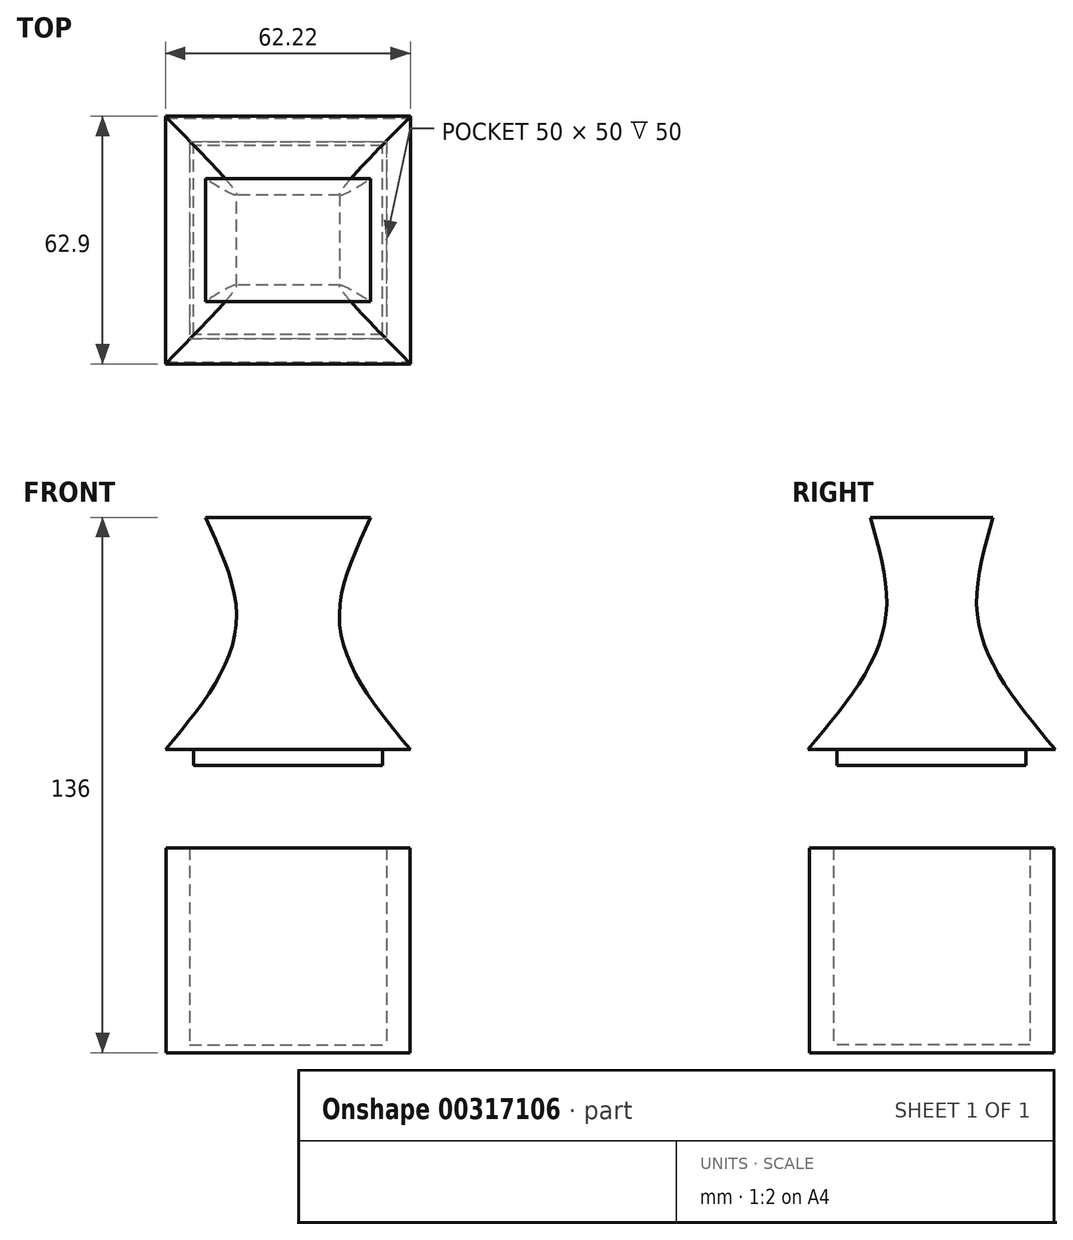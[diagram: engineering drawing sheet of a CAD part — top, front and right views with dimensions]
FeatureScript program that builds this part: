
annotation { "Feature Type Name" : "Feature", "Feature Type Description" : "" }
export const myFeature = defineFeature(function(context is Context, id is Id, definition is map)
    precondition{}
    {
        {
            var Q0;
            Q0=qCreatedBy(makeId("Top.planeOp"),FACE);
            var sketch = newSketch(context, id + "F0", { "sketchPlane" : qUnion([Q0])});
            skLineSegment(sketch, "E0.bottom", {"start": v(-25, 25) * mm, "end": v(25, 25) * mm});
            skLineSegment(sketch, "E0.top", {"start": v(-25, -25) * mm, "end": v(25, -25) * mm});
            skLineSegment(sketch, "E0.left", {"start": v(-25, 25) * mm, "end": v(-25, -25) * mm});
            skLineSegment(sketch, "E0.right", {"start": v(25, 25) * mm, "end": v(25, -25) * mm});
            skPoint(sketch, "E0.middle", {"position": v(0, 0) * mm});
            skLineSegment(sketch, "E1.0", {"start": v(-31, 31) * mm, "end": v(31, 31) * mm});
            skLineSegment(sketch, "E1.1", {"start": v(-31, 31) * mm, "end": v(-31, -31) * mm});
            skLineSegment(sketch, "E1.2", {"start": v(-31, -31) * mm, "end": v(31, -31) * mm});
            skLineSegment(sketch, "E1.3", {"start": v(31, 31) * mm, "end": v(31, -31) * mm});
            skSolve(sketch);
        }
        {
            var Q0;
            Q0=makeQuery(id+"F0.imprint","IMPRINT",FACE,{"disambiguationData":[TD([[makeQuery(id+"F0.imprint","IMPRINT",EDGE,{"derivedFrom":sQuery(id+"F0.wireOp",EDGE,"E0.bottom")}),1.0]])]});
            extrude(context, id + "F1", {"entities" : qUnion([Q0]), "depth" : 50 * mm});
        }
        {
            var Q0;
            Q0=makeQuery(id+"F0.imprint","IMPRINT",FACE,{"disambiguationData":[TD([[makeQuery(id+"F0.imprint","IMPRINT",EDGE,{"derivedFrom":sQuery(id+"F0.wireOp",EDGE,"E0.bottom")}),-1.0]])]});
            var Q1;
            Q1=makeQuery(id+"F0.imprint","IMPRINT",FACE,{"disambiguationData":[TD([[makeQuery(id+"F0.imprint","IMPRINT",EDGE,{"derivedFrom":sQuery(id+"F0.wireOp",EDGE,"E0.bottom")}),1.0]])]});
            extrude(context, id + "F2", {"entities" : qUnion([Q0, Q1]), "operationType" : NewBodyOperationType.ADD, "oppositeDirection" : true, "depth" : 2 * mm});
        }
        {
            var Q0;
            Q0=makeQuery(id+"F1.opExtrude","CAP_FACE",FACE,{"disambiguationData":[OSD([sQuery(id+"F0.wireOp",EDGE,"E0.bottom"),sQuery(id+"F0.wireOp",EDGE,"E0.top"),sQuery(id+"F0.wireOp",EDGE,"E0.left"),sQuery(id+"F0.wireOp",EDGE,"E0.right"),sQuery(id+"F0.wireOp",EDGE,"E1.0"),sQuery(id+"F0.wireOp",EDGE,"E1.1"),sQuery(id+"F0.wireOp",EDGE,"E1.2"),sQuery(id+"F0.wireOp",EDGE,"E1.3")])],"isStart":false});
            cPlane(context, id + "F3", {"entities" : qUnion([Q0]), "cplaneType" : CPlaneType.OFFSET, "offset" : 25 * mm, "width" : 150 * mm, "height" : 150 * mm});
        }
        {
            var Q0;
            Q0=qCreatedBy(id+"F3.planeOp",FACE);
            var sketch = newSketch(context, id + "F4", { "sketchPlane" : qUnion([Q0])});
            skLineSegment(sketch, "E2.bottom", {"start": v(-31.1, 31.45) * mm, "end": v(31.1, 31.45) * mm});
            skLineSegment(sketch, "E2.top", {"start": v(-31.1, -31.45) * mm, "end": v(31.1, -31.45) * mm});
            skLineSegment(sketch, "E2.left", {"start": v(-31.1, 31.45) * mm, "end": v(-31.1, -31.45) * mm});
            skLineSegment(sketch, "E2.right", {"start": v(31.1, 31.45) * mm, "end": v(31.1, -31.45) * mm});
            skPoint(sketch, "E2.middle", {"position": v(0, 0) * mm});
            skSolve(sketch);
        }
        {
            var Q0;
            Q0=qCreatedBy(id+"F3.planeOp",FACE);
            cPlane(context, id + "F5", {"entities" : qUnion([Q0]), "cplaneType" : CPlaneType.OFFSET, "offset" : 34 * mm, "width" : 150 * mm, "height" : 150 * mm});
        }
        {
            var Q0;
            Q0=qCreatedBy(id+"F5.planeOp",FACE);
            var sketch = newSketch(context, id + "F6", { "sketchPlane" : qUnion([Q0])});
            skLineSegment(sketch, "E3.bottom", {"start": v(13.05, 11.6) * mm, "end": v(-13.05, 11.6) * mm});
            skLineSegment(sketch, "E3.top", {"start": v(13.05, -11.6) * mm, "end": v(-13.05, -11.6) * mm});
            skLineSegment(sketch, "E3.left", {"start": v(13.05, 11.6) * mm, "end": v(13.05, -11.6) * mm});
            skLineSegment(sketch, "E3.right", {"start": v(-13.05, 11.6) * mm, "end": v(-13.05, -11.6) * mm});
            skPoint(sketch, "E3.middle", {"position": v(0, 0) * mm});
            skSolve(sketch);
        }
        {
            var Q0;
            Q0=qCreatedBy(id+"F5.planeOp",FACE);
            cPlane(context, id + "F7", {"entities" : qUnion([Q0]), "cplaneType" : CPlaneType.OFFSET, "offset" : 25 * mm, "width" : 150 * mm, "height" : 150 * mm});
        }
        {
            var Q0;
            Q0=qCreatedBy(id+"F7.planeOp",FACE);
            var sketch = newSketch(context, id + "F8", { "sketchPlane" : qUnion([Q0])});
            skLineSegment(sketch, "E4.bottom", {"start": v(21, 15.6) * mm, "end": v(-21, 15.6) * mm});
            skLineSegment(sketch, "E4.top", {"start": v(21, -15.6) * mm, "end": v(-21, -15.6) * mm});
            skLineSegment(sketch, "E4.left", {"start": v(21, 15.6) * mm, "end": v(21, -15.6) * mm});
            skLineSegment(sketch, "E4.right", {"start": v(-21, 15.6) * mm, "end": v(-21, -15.6) * mm});
            skPoint(sketch, "E4.middle", {"position": v(0, 0) * mm});
            skSolve(sketch);
        }
        {
            var Q0;
            Q0=makeQuery(id+"F4.imprint","IMPRINT",FACE,{"disambiguationData":[TD([[makeQuery(id+"F4.imprint","IMPRINT",EDGE,{"derivedFrom":sQuery(id+"F4.wireOp",EDGE,"E2.bottom")}),-1.0]])]});
            var Q1;
            Q1=makeQuery(id+"F6.imprint","IMPRINT",FACE,{"disambiguationData":[TD([[makeQuery(id+"F6.imprint","IMPRINT",EDGE,{"derivedFrom":sQuery(id+"F6.wireOp",EDGE,"E3.bottom")}),1.0]])]});
            var Q2;
            Q2=makeQuery(id+"F8.imprint","IMPRINT",FACE,{"disambiguationData":[TD([[makeQuery(id+"F8.imprint","IMPRINT",EDGE,{"derivedFrom":sQuery(id+"F8.wireOp",EDGE,"E4.bottom")}),1.0]])]});
            loft(context, id + "F9", {"sheetProfilesArray" : [{ "sheetProfileEntities" : qUnion([Q0]) }, { "sheetProfileEntities" : qUnion([Q1]) }, { "sheetProfileEntities" : qUnion([Q2]) }]});
        }
        {
            var Q0;
            Q0=makeQuery(id+"F9.opLoft","CAP_FACE",FACE,{"disambiguationData":[OSD([makeQuery(id+"F4.imprint","IMPRINT",FACE,{"disambiguationData":[TD([[makeQuery(id+"F4.imprint","IMPRINT",EDGE,{"derivedFrom":sQuery(id+"F4.wireOp",EDGE,"E2.bottom")}),-1.0]])]})])],"isStart":true});
            var sketch = newSketch(context, id + "F10", { "sketchPlane" : qUnion([Q0])});
            skLineSegment(sketch, "E5.bottom", {"start": v(24, 24) * mm, "end": v(-24, 24) * mm});
            skLineSegment(sketch, "E5.top", {"start": v(24, -24) * mm, "end": v(-24, -24) * mm});
            skLineSegment(sketch, "E5.left", {"start": v(24, 24) * mm, "end": v(24, -24) * mm});
            skLineSegment(sketch, "E5.right", {"start": v(-24, 24) * mm, "end": v(-24, -24) * mm});
            skPoint(sketch, "E5.middle", {"position": v(0, 0) * mm});
            skSolve(sketch);
        }
        {
            var Q0;
            Q0=makeQuery(id+"F10.imprint","IMPRINT",FACE,{"disambiguationData":[TD([[makeQuery(id+"F10.imprint","IMPRINT",EDGE,{"derivedFrom":sQuery(id+"F10.wireOp",EDGE,"E5.bottom")}),1.0]])]});
            extrude(context, id + "F11", {"entities" : qUnion([Q0]), "operationType" : NewBodyOperationType.ADD, "depth" : 4 * mm});
        }
    });
